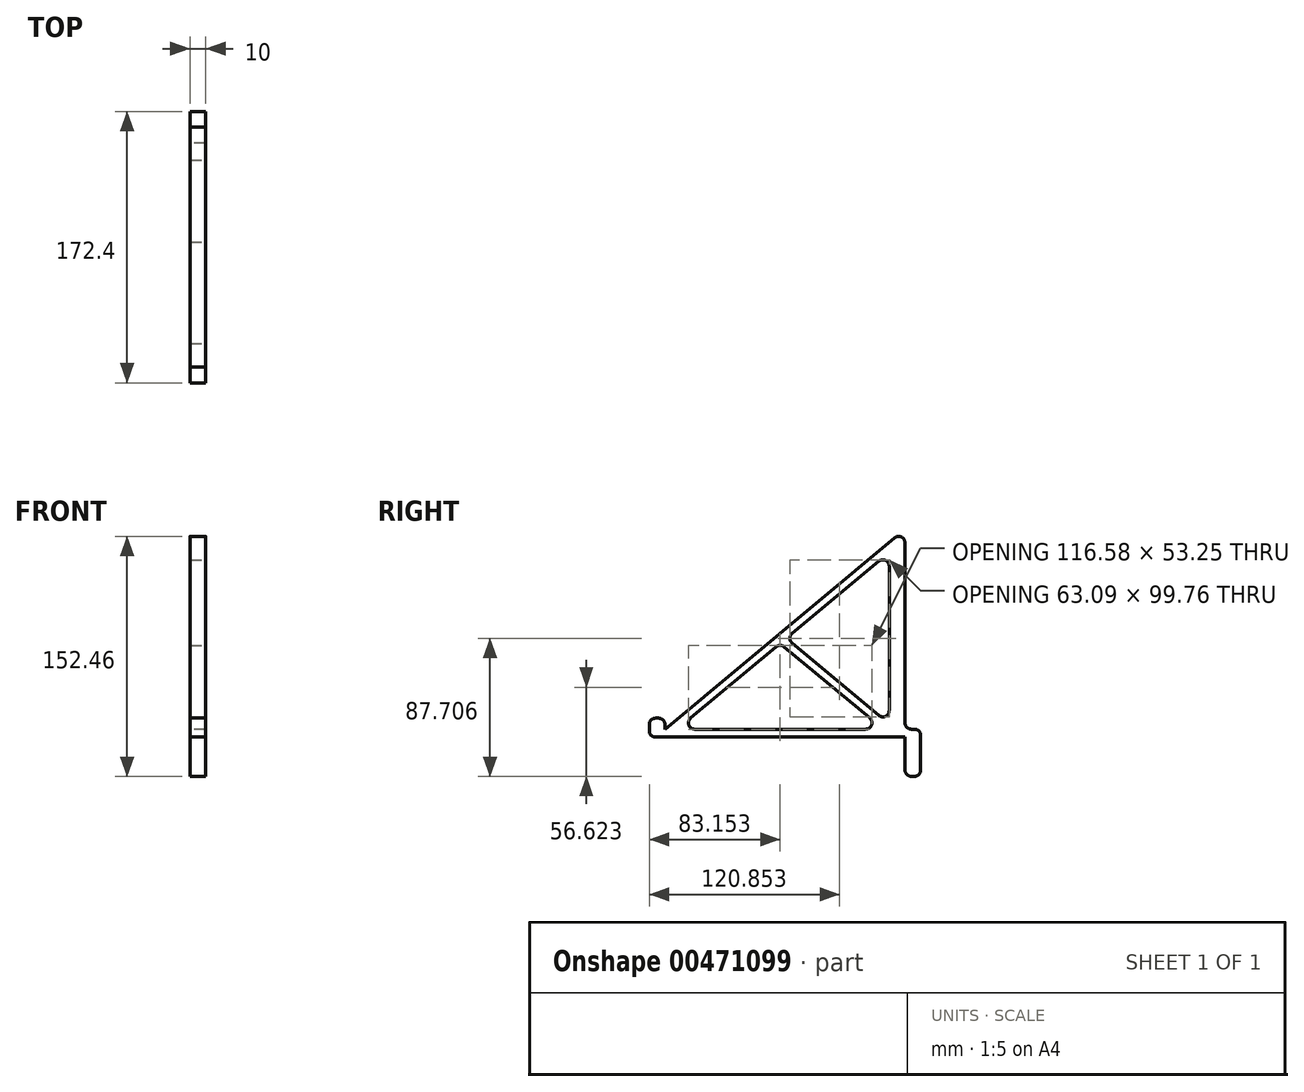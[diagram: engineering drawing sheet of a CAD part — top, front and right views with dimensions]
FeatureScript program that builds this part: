
annotation { "Feature Type Name" : "Feature", "Feature Type Description" : "" }
export const myFeature = defineFeature(function(context is Context, id is Id, definition is map)
    precondition{}
    {
        {
            var Q0;
            Q0=qCreatedBy(makeId("Right.planeOp"),FACE);
            var sketch = newSketch(context, id + "F0", { "sketchPlane" : qUnion([Q0])});
            skLineSegment(sketch, "E0.bottom", {"start": v(-152.4, 0) * mm, "end": v(0, 0) * mm});
            skLineSegment(sketch, "E0.top", {"start": v(-152.4, 5) * mm, "end": v(0, 5) * mm});
            skLineSegment(sketch, "E0.left", {"start": v(-152.4, 0) * mm, "end": v(-152.4, 5) * mm});
            skLineSegment(sketch, "E0.right", {"start": v(0, 0) * mm, "end": v(0, 5) * mm});
            skLineSegment(sketch, "E1.bottom", {"start": v(-152.4, 0) * mm, "end": v(-162.4, 0) * mm});
            skLineSegment(sketch, "E1.top", {"start": v(-152.4, 12) * mm, "end": v(-162.4, 12) * mm});
            skLineSegment(sketch, "E1.left", {"start": v(-152.4, 0) * mm, "end": v(-152.4, 12) * mm, "construction": true});
            skLineSegment(sketch, "E1.right", {"start": v(-162.4, 0) * mm, "end": v(-162.4, 12) * mm});
            skLineSegment(sketch, "E2.bottom", {"start": v(0, 5) * mm, "end": v(10, 5) * mm});
            skLineSegment(sketch, "E2.top", {"start": v(0, -25) * mm, "end": v(10, -25) * mm});
            skLineSegment(sketch, "E2.left", {"start": v(0, 5) * mm, "end": v(0, -25) * mm});
            skLineSegment(sketch, "E2.right", {"start": v(10, 5) * mm, "end": v(10, -25) * mm});
            skLineSegment(sketch, "E3", {"start": v(-152.4, 12) * mm, "end": v(-152.4, 5) * mm});
            skLineSegment(sketch, "E4", {"start": v(0, 0) * mm, "end": v(0, -25) * mm});
            skLineSegment(sketch, "E5", {"start": v(0, 5) * mm, "end": v(0, 132) * mm});
            skLineSegment(sketch, "E6", {"start": v(0, 132) * mm, "end": v(-152.4, 5) * mm});
            skLineSegment(sketch, "E7", {"start": v(-10, 5) * mm, "end": v(-10, 117.16) * mm});
            skLineSegment(sketch, "E8", {"start": v(-10, 117.16) * mm, "end": v(-144.59, 5) * mm});
            skLineSegment(sketch, "E9", {"start": v(-10, 5) * mm, "end": v(-77.3, 61.08) * mm, "construction": true});
            skLineSegment(sketch, "E10", {"start": v(-13.9, 5) * mm, "end": v(-79.25, 59.45) * mm});
            skLineSegment(sketch, "E11", {"start": v(-75.34, 62.7) * mm, "end": v(-10, 8.25) * mm});
            skSolve(sketch);
        }
        {
            var Q0;
            Q0=makeQuery(id+"F0.imprint","IMPRINT",FACE,{"disambiguationData":[TD([[makeQuery(id+"F0.imprint","IMPRINT",EDGE,{"derivedFrom":sQuery(id+"F0.wireOp",EDGE,"E0.left")}),1.0]])]});
            var Q1;
            Q1=makeQuery(id+"F0.imprint","IMPRINT",FACE,{"disambiguationData":[TD([[makeQuery(id+"F0.imprint","IMPRINT",EDGE,{"derivedFrom":sQuery(id+"F0.wireOp",EDGE,"E2.bottom")}),-1.0]])]});
            var Q2;
            Q2=makeQuery(id+"F0.imprint","IMPRINT",FACE,{"disambiguationData":[TD([[makeQuery(id+"F0.imprint","IMPRINT",EDGE,{"derivedFrom":sQuery(id+"F0.wireOp",EDGE,"E0.bottom")}),1.0]])]});
            var Q3;
            {var subQ0=sQuery(id+"F0.wireOp",EDGE,"E5");Q3=makeQuery(id+"F0.imprint","IMPRINT",FACE,{"disambiguationData":[TD([[makeQuery(id+"F0.imprint","IMPRINT",EDGE,{"derivedFrom":subQ0}),1.0]])]});}
            var Q4;
            {var subQ0=sQuery(id+"F0.wireOp",EDGE,"E10");Q4=makeQuery(id+"F0.imprint","IMPRINT",FACE,{"disambiguationData":[TD([[makeQuery(id+"F0.imprint","IMPRINT",EDGE,{"derivedFrom":subQ0}),-1.0]])]});}
            extrude(context, id + "F1", {"entities" : qUnion([Q0, Q1, Q2, Q3, Q4]), "depth" : 10 * mm});
        }
        {
            var Q0;
            Q0=makeQuery(id+"F1.opExtrude","SWEPT_EDGE",EDGE,{"disambiguationData":[OSD([sQuery(id+"F0.wireOp",EDGE,"E1.top"),sQuery(id+"F0.wireOp",EDGE,"E1.right")])]});
            var Q1;
            Q1=makeQuery(id+"F1.opExtrude","SWEPT_EDGE",EDGE,{"disambiguationData":[OSD([sQuery(id+"F0.wireOp",EDGE,"E1.top"),sQuery(id+"F0.wireOp",EDGE,"E3")])]});
            var Q2;
            Q2=makeQuery(id+"F1.opExtrude","SWEPT_EDGE",EDGE,{"disambiguationData":[OSD([sQuery(id+"F0.wireOp",EDGE,"E2.bottom"),sQuery(id+"F0.wireOp",EDGE,"E2.right")])]});
            var Q3;
            Q3=makeQuery(id+"F1.opExtrude","SWEPT_EDGE",EDGE,{"disambiguationData":[OSD([sQuery(id+"F0.wireOp",EDGE,"E2.top"),sQuery(id+"F0.wireOp",EDGE,"E4")])]});
            var Q4;
            Q4=makeQuery(id+"F1.opExtrude","SWEPT_EDGE",EDGE,{"disambiguationData":[OSD([sQuery(id+"F0.wireOp",EDGE,"E2.top"),sQuery(id+"F0.wireOp",EDGE,"E2.right")])]});
            var Q5;
            Q5=makeQuery(id+"F1.opExtrude","SWEPT_EDGE",EDGE,{"disambiguationData":[OSD([sQuery(id+"F0.wireOp",EDGE,"E1.bottom"),sQuery(id+"F0.wireOp",EDGE,"E1.right")])]});
            var Q6;
            Q6=makeQuery(id+"F1.opExtrude","SWEPT_EDGE",EDGE,{"disambiguationData":[OSD([sQuery(id+"F0.wireOp",EDGE,"E5"),sQuery(id+"F0.wireOp",EDGE,"E6")])]});
            var Q7;
            Q7=makeQuery(id+"F1.opExtrude","SWEPT_EDGE",EDGE,{"disambiguationData":[OSD([sQuery(id+"F0.wireOp",EDGE,"E8"),sQuery(id+"F0.wireOp",EDGE,"E11")])]});
            var Q8;
            Q8=makeQuery(id+"F1.opExtrude","SWEPT_EDGE",EDGE,{"disambiguationData":[OSD([sQuery(id+"F0.wireOp",EDGE,"E8"),sQuery(id+"F0.wireOp",EDGE,"E10")])]});
            var Q9;
            Q9=makeQuery(id+"F1.opExtrude","SWEPT_EDGE",EDGE,{"disambiguationData":[OSD([sQuery(id+"F0.wireOp",EDGE,"E7"),sQuery(id+"F0.wireOp",EDGE,"E8")])]});
            var Q10;
            Q10=makeQuery(id+"F1.opExtrude","SWEPT_EDGE",EDGE,{"disambiguationData":[OSD([sQuery(id+"F0.wireOp",EDGE,"E0.top"),sQuery(id+"F0.wireOp",EDGE,"E8")])]});
            var Q11;
            Q11=makeQuery(id+"F1.opExtrude","SWEPT_EDGE",EDGE,{"disambiguationData":[OSD([sQuery(id+"F0.wireOp",EDGE,"E0.top"),sQuery(id+"F0.wireOp",EDGE,"E10")])]});
            var Q12;
            Q12=makeQuery(id+"F1.opExtrude","SWEPT_EDGE",EDGE,{"disambiguationData":[OSD([sQuery(id+"F0.wireOp",EDGE,"E7"),sQuery(id+"F0.wireOp",EDGE,"E11")])]});
            var Q13;
            Q13=makeQuery(id+"F1.opExtrude","SWEPT_EDGE",EDGE,{"disambiguationData":[OSD([sQuery(id+"F0.wireOp",EDGE,"E0.top"),sQuery(id+"F0.wireOp",EDGE,"E2.bottom"),sQuery(id+"F0.wireOp",EDGE,"E2.left"),sQuery(id+"F0.wireOp",EDGE,"E5")])]});
            fillet(context, id + "F2", {"entities" : qUnion([Q0, Q1, Q2, Q3, Q4, Q5, Q6, Q7, Q8, Q9, Q10, Q11, Q12, Q13]), "radius" : 4 * mm, "tangentPropagation" : true, "allowEdgeOverflow" : false});
        }
    });
